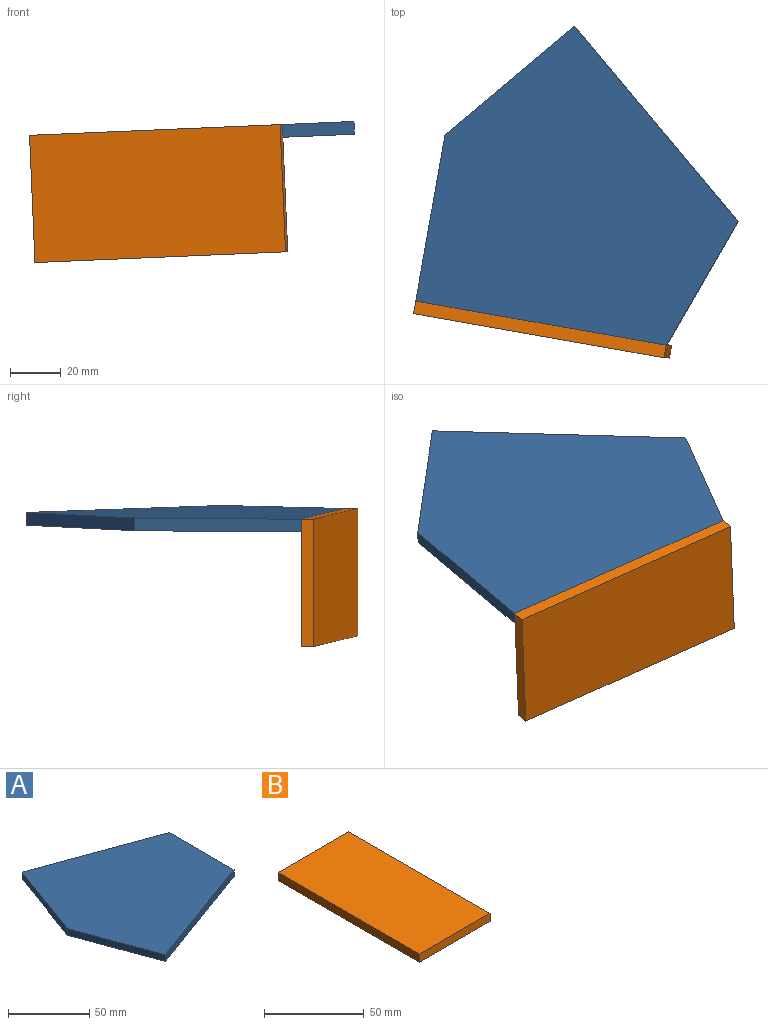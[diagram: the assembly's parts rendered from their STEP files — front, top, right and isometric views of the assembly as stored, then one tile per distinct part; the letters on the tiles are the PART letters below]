
ASSEMBLY  parts=2 mates=1
PART A: 7 faces, bbox 116.7x124.7x5 mm
  f0: plane 93.97x34.2mm, normal (0.34,-0.94,0), area 500mm2, adj f1,f4,f5,f6
  f1: plane 56.33x5mm, normal (1,0,0), area 281.7mm2, adj f0,f2,f5,f6
  f2: plane 93.97x34.2mm, normal (0.34,0.94,0), area 500mm2, adj f1,f3,f5,f6
  f3: plane 62.37x22.7mm, normal (-0.94,0.34,0), area 331.8mm2, adj f2,f4,f5,f6
  f4: plane 62.37x22.7mm, normal (-0.94,-0.34,0), area 331.8mm2, adj f0,f3,f5,f6
  f5: plane 124.73x116.67mm, normal (0,0,1), area 9922.9mm2, adj f0,f1,f2,f3,f4
  f6: plane 124.73x116.67mm, normal (0,0,-1), area 9922.9mm2, adj f0,f1,f2,f3,f4
PART B: 6 faces, bbox 50x100x5 mm
  f0: plane 50x5mm, normal (0,-1,0), area 250mm2, adj f1,f3,f4,f5
  f1: plane 100x5mm, normal (1,0,0), area 500mm2, adj f0,f2,f4,f5
  f2: plane 50x5mm, normal (0,1,0), area 250mm2, adj f1,f3,f4,f5
  f3: plane 100x5mm, normal (-1,0,0), area 500mm2, adj f0,f2,f4,f5
  f4: plane 100x50mm, normal (0,0,1), area 5000mm2, adj f0,f1,f2,f3
  f5: plane 100x50mm, normal (0,0,-1), area 5000mm2, adj f0,f1,f2,f3
PLACE A rot(axis=(0.02,-0.08,-1),30.1deg) t=(145.34,-25.47,50.95)mm
PLACE B rot(axis=(-0.56,0.64,0.53),112.8deg) t=(17.17,-8.61,25.45)mm
MATE fastened A.f0 <-> B.f4  axis (-0.17,-0.98,-0.01) through (16.97,-3.68,50.46)mm
